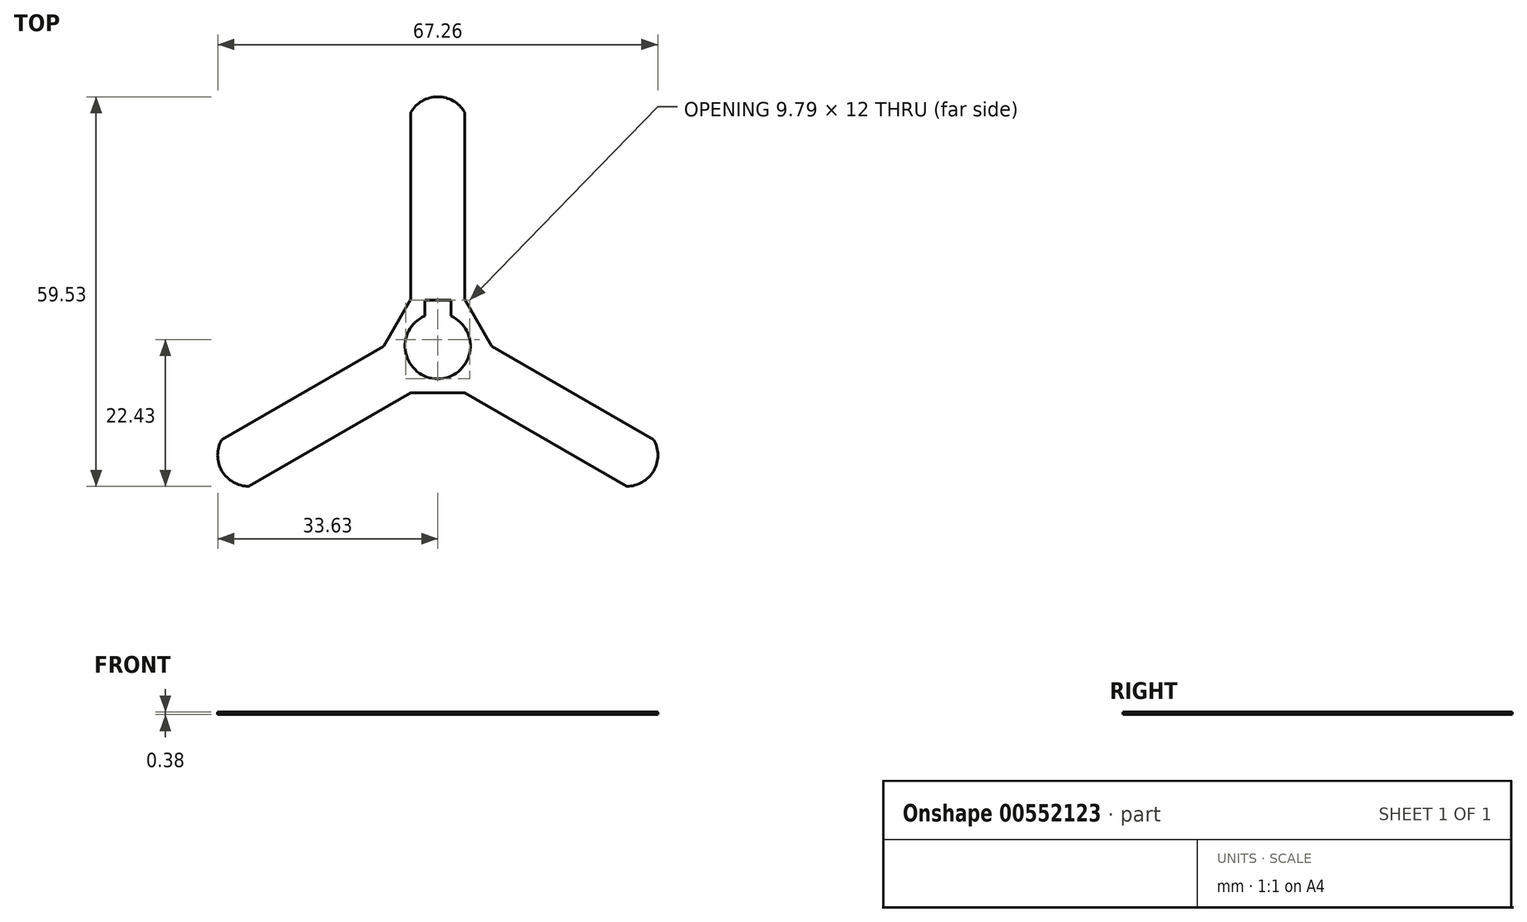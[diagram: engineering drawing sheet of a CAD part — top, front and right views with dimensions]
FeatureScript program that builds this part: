
annotation { "Feature Type Name" : "Feature", "Feature Type Description" : "" }
export const myFeature = defineFeature(function(context is Context, id is Id, definition is map)
    precondition{}
    {
        {
            assignVariable(context, id + "F0", {"name" : "AT", "anyValue" : 3 / 8});
        }
        {
            var Q0;
            Q0=qCreatedBy(makeId("Top.planeOp"),FACE);
            var sketch = newSketch(context, id + "F1", { "sketchPlane" : qUnion([Q0])});
            skCircle(sketch, "E0.cCircle", {"center": v(0, 0) * mm, "radius": 42.86 * mm, "construction": true});
            skLineSegment(sketch, "E0.0", {"start": v(4.12, 35.72) * mm, "end": v(33, -14.29) * mm});
            skLineSegment(sketch, "E0.1", {"start": v(28.87, -21.43) * mm, "end": v(-28.87, -21.43) * mm});
            skLineSegment(sketch, "E0.2", {"start": v(-33, -14.29) * mm, "end": v(-4.12, 35.72) * mm});
            skPoint(sketch, "E1.visualSharp", {"position": v(0, 42.86) * mm});
            skArc(sketch, "E1.filletArc", {"start": v(4.12, 35.72) * mm, "mid": v(0, 38.1) * mm, "end": v(-4.12, 35.72) * mm});
            skPoint(sketch, "E2.visualSharp", {"position": v(37.12, -21.43) * mm});
            skArc(sketch, "E2.filletArc", {"start": v(28.87, -21.43) * mm, "mid": v(33, -19.05) * mm, "end": v(33, -14.29) * mm});
            skPoint(sketch, "E3.visualSharp", {"position": v(-37.12, -21.43) * mm});
            skArc(sketch, "E3.filletArc", {"start": v(-33, -14.29) * mm, "mid": v(-33, -19.05) * mm, "end": v(-28.87, -21.43) * mm});
            skPoint(sketch, "E4", {"position": v(-8.25, 0) * mm});
            skPoint(sketch, "E5", {"position": v(8.25, 0) * mm});
            skPoint(sketch, "E6", {"position": v(-4.12, -7.14) * mm});
            skPoint(sketch, "E7", {"position": v(4.12, -7.14) * mm});
            skPoint(sketch, "E8", {"position": v(4.12, 7.14) * mm});
            skPoint(sketch, "E9", {"position": v(-4.12, 7.14) * mm});
            skLineSegment(sketch, "E10", {"start": v(-28.87, -21.43) * mm, "end": v(-4.12, -7.14) * mm});
            skLineSegment(sketch, "E11", {"start": v(-33, -14.29) * mm, "end": v(-8.25, 0) * mm});
            skLineSegment(sketch, "E12", {"start": v(-4.12, 35.72) * mm, "end": v(-4.12, 7.14) * mm});
            skLineSegment(sketch, "E13", {"start": v(4.12, 7.14) * mm, "end": v(4.12, 35.72) * mm});
            skLineSegment(sketch, "E14", {"start": v(8.25, 0) * mm, "end": v(33, -14.29) * mm});
            skLineSegment(sketch, "E15", {"start": v(28.87, -21.43) * mm, "end": v(4.12, -7.14) * mm});
            skLineSegment(sketch, "E16", {"start": v(4.12, -7.14) * mm, "end": v(-4.12, -7.14) * mm});
            skLineSegment(sketch, "E17", {"start": v(-8.25, 0) * mm, "end": v(-4.12, 7.14) * mm});
            skLineSegment(sketch, "E18", {"start": v(4.12, 7.14) * mm, "end": v(8.25, 0) * mm});
            skCircle(sketch, "E19", {"center": v(0, 0) * mm, "radius": 5 * mm});
            skLineSegment(sketch, "E20", {"start": v(0, 5) * mm, "end": v(0, 3) * mm});
            skLineSegment(sketch, "E21", {"start": v(0, 3) * mm, "end": v(2, 3) * mm});
            skLineSegment(sketch, "E22", {"start": v(0, 3) * mm, "end": v(-2, 3) * mm});
            skLineSegment(sketch, "E23", {"start": v(-2, 3) * mm, "end": v(-2, 7) * mm});
            skLineSegment(sketch, "E24", {"start": v(-2, 7) * mm, "end": v(2, 7) * mm});
            skLineSegment(sketch, "E25", {"start": v(2, 7) * mm, "end": v(2, 3) * mm});
            skPoint(sketch, "E26", {"position": v(0, 5) * mm});
            skLineSegment(sketch, "E27", {"start": v(-2, 7) * mm, "end": v(2, 3) * mm});
            skSolve(sketch);
        }
        {
            var Q0;
            Q0=makeQuery(id+"F1.imprint","IMPRINT",FACE,{"disambiguationData":[TD([[makeQuery(id+"F1.imprint","IMPRINT",EDGE,{"derivedFrom":sQuery(id+"F1.wireOp",EDGE,"E1.filletArc")}),1.0]])]});
            extrude(context, id + "F2", {"entities" : qUnion([Q0]), "depth" : (getVariable(context, 'AT')) * mm, "offsetDistance" : 25.4 * mm});
        }
    });
